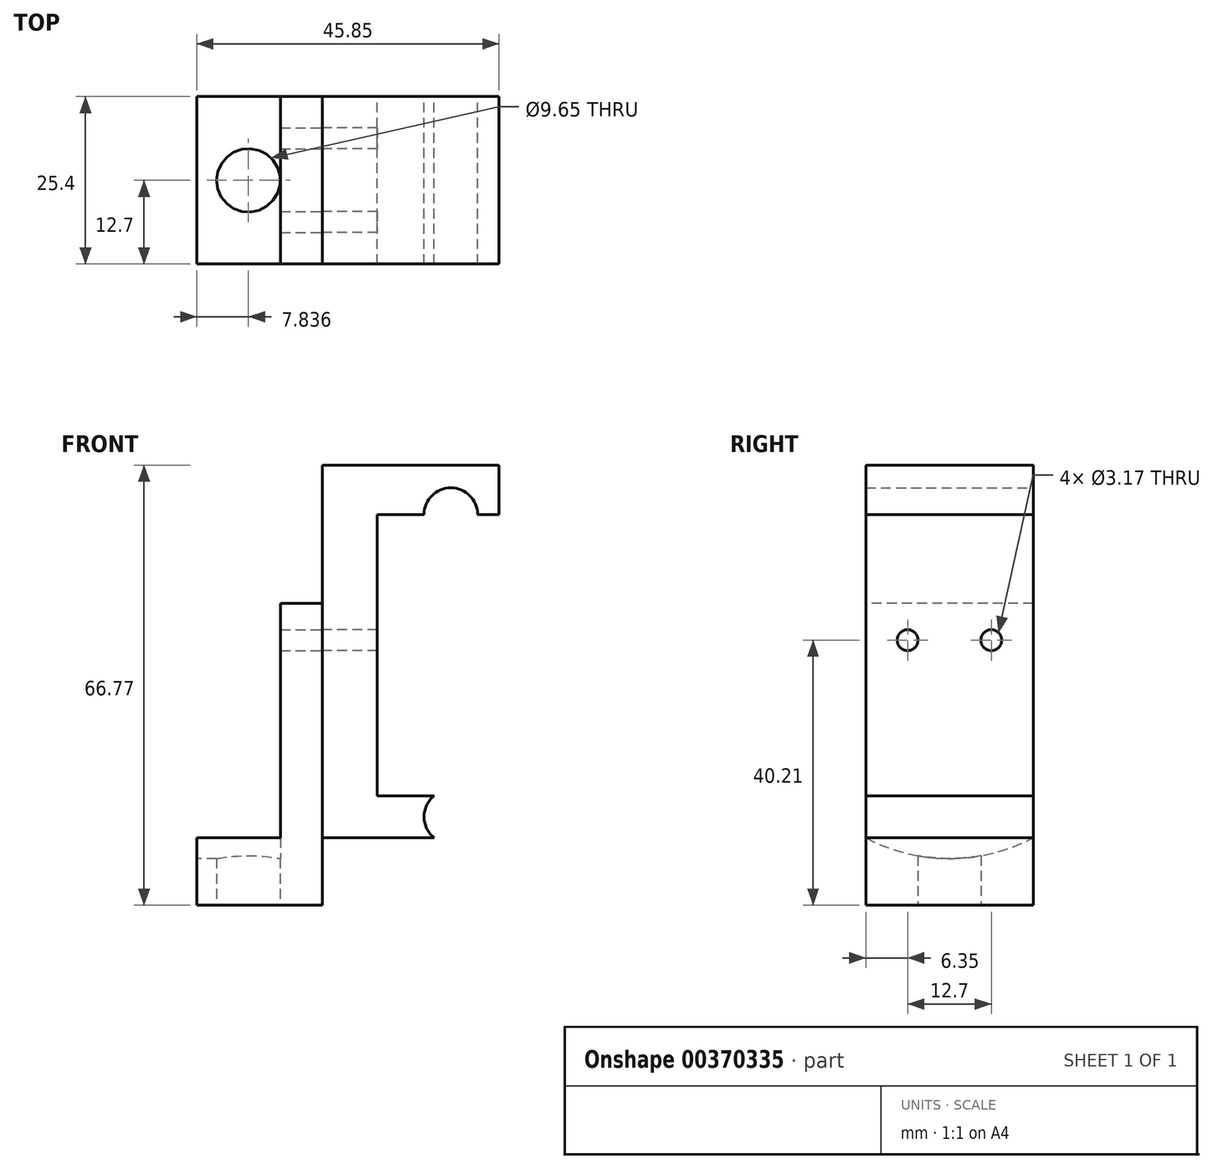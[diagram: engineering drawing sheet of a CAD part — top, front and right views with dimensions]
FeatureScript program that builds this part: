
annotation { "Feature Type Name" : "Feature", "Feature Type Description" : "" }
export const myFeature = defineFeature(function(context is Context, id is Id, definition is map)
    precondition{}
    {
        {
            var Q0;
            Q0=qCreatedBy(makeId("Front.planeOp"),FACE);
            var sketch = newSketch(context, id + "F0", { "sketchPlane" : qUnion([Q0])});
            skCircle(sketch, "E0", {"center": v(0, 0) * mm, "radius": 4.06 * mm, "construction": true});
            skCircle(sketch, "E1", {"center": v(0, -45.85) * mm, "radius": 4.06 * mm, "construction": true});
            skLineSegment(sketch, "E2", {"start": v(4.06, 0) * mm, "end": v(7.3, 0) * mm});
            skLineSegment(sketch, "E3", {"start": v(7.3, 0) * mm, "end": v(7.3, 7.51) * mm});
            skArc(sketch, "E4", {"start": v(4.06, 0) * mm, "mid": v(0, 4.06) * mm, "end": v(-4.06, 0) * mm});
            skLineSegment(sketch, "E5", {"start": v(-2.52, -42.66) * mm, "end": v(-2.52, -49.04) * mm, "construction": true});
            skArc(sketch, "E6", {"start": v(-2.52, -42.66) * mm, "mid": v(-4.06, -45.85) * mm, "end": v(-2.52, -49.04) * mm});
            skLineSegment(sketch, "E7", {"start": v(-2.52, -42.66) * mm, "end": v(-11.15, -42.66) * mm});
            skLineSegment(sketch, "E8", {"start": v(-11.15, -42.66) * mm, "end": v(-11.15, 0) * mm});
            skLineSegment(sketch, "E9", {"start": v(-11.15, 0) * mm, "end": v(-4.06, 0) * mm});
            skLineSegment(sketch, "E10", {"start": v(7.3, 7.51) * mm, "end": v(-19.5, 7.51) * mm});
            skLineSegment(sketch, "E11", {"start": v(-19.5, 7.51) * mm, "end": v(-19.5, -49.04) * mm});
            skLineSegment(sketch, "E12", {"start": v(-19.5, -49.04) * mm, "end": v(-2.52, -49.04) * mm});
            skSolve(sketch);
        }
        {
            var Q0;
            Q0 = qSketchRegion(id + "F0", true);
            extrude(context, id + "F1", {"entities" : qUnion([Q0]), "endBound" : BoundingType.SYMMETRIC, "depth" : 25.4 * mm});
        }
        {
            var Q0;
            Q0=makeQuery(id+"F1.opExtrude","SWEPT_FACE",FACE,{"disambiguationData":[OSD([sQuery(id+"F0.wireOp",EDGE,"E11")])]});
            var sketch = newSketch(context, id + "F2", { "sketchPlane" : qUnion([Q0])});
            skCircle(sketch, "E13", {"center": v(-6.35, -19.05) * mm, "radius": 1.59 * mm});
            skCircle(sketch, "E14", {"center": v(6.35, -19.05) * mm, "radius": 1.59 * mm});
            skSolve(sketch);
        }
        {
            var Q0;
            Q0 = qSketchRegion(id + "F2", true);
            extrude(context, id + "F3", {"entities" : qUnion([Q0]), "operationType" : NewBodyOperationType.REMOVE, "endBound" : BoundingType.THROUGH_ALL, "oppositeDirection" : true, "depth" : 25.4 * mm});
        }
        {
            var Q0;
            Q0=makeQuery(id+"F1.opExtrude","SWEPT_FACE",FACE,{"disambiguationData":[OSD([sQuery(id+"F0.wireOp",EDGE,"E11")])]});
            var sketch = newSketch(context, id + "F4", { "sketchPlane" : qUnion([Q0])});
            skLineSegment(sketch, "E15.bottom", {"start": v(-12.7, -13.48) * mm, "end": v(12.7, -13.48) * mm});
            skLineSegment(sketch, "E15.top", {"start": v(-12.7, -59.26) * mm, "end": v(12.7, -59.26) * mm});
            skLineSegment(sketch, "E15.left", {"start": v(-12.7, -13.48) * mm, "end": v(-12.7, -59.26) * mm});
            skLineSegment(sketch, "E15.right", {"start": v(12.7, -13.48) * mm, "end": v(12.7, -59.26) * mm});
            skCircle(sketch, "E16", {"center": v(-6.35, -19.05) * mm, "radius": 1.59 * mm});
            skCircle(sketch, "E17", {"center": v(6.35, -19.05) * mm, "radius": 1.59 * mm});
            skSolve(sketch);
        }
        {
            var Q0;
            Q0 = qSketchRegion(id + "F4", true);
            extrude(context, id + "F5", {"entities" : qUnion([Q0]), "depth" : 19.05 * mm});
        }
        {
            var Q0;
            Q0=makeQuery(id+"F5.opExtrude","CAP_FACE",FACE,{"disambiguationData":[OSD([sQuery(id+"F4.wireOp",EDGE,"E15.bottom"),sQuery(id+"F4.wireOp",EDGE,"E15.top"),sQuery(id+"F4.wireOp",EDGE,"E15.left"),sQuery(id+"F4.wireOp",EDGE,"E15.right"),sQuery(id+"F4.wireOp",EDGE,"E16"),sQuery(id+"F4.wireOp",EDGE,"E17")])],"isStart":false});
            var sketch = newSketch(context, id + "F6", { "sketchPlane" : qUnion([Q0])});
            skCircle(sketch, "E18", {"center": v(0, -24.88) * mm, "radius": 27.3 * mm});
            skSolve(sketch);
        }
        {
            var Q0;
            Q0 = qSketchRegion(id + "F6", true);
            var Q1;
            Q1=makeQuery(id+"F1.opExtrude","SWEPT_FACE",FACE,{"disambiguationData":[OSD([sQuery(id+"F0.wireOp",EDGE,"E11")])]});
            extrude(context, id + "F7", {"entities" : qUnion([Q0]), "operationType" : NewBodyOperationType.REMOVE, "oppositeDirection" : true, "endBoundEntityFace" : qUnion([Q1]), "depth" : 12.7 * mm});
        }
        {
            var Q0;
            Q0=makeQuery(id+"F5.opExtrude","SWEPT_FACE",FACE,{"disambiguationData":[OSD([sQuery(id+"F4.wireOp",EDGE,"E15.top")])]});
            var sketch = newSketch(context, id + "F8", { "sketchPlane" : qUnion([Q0])});
            skCircle(sketch, "E19", {"center": v(-30.71, 0) * mm, "radius": 4.83 * mm});
            skSolve(sketch);
        }
        {
            var Q0;
            Q0 = qSketchRegion(id + "F8", true);
            extrude(context, id + "F9", {"entities" : qUnion([Q0]), "operationType" : NewBodyOperationType.REMOVE, "oppositeDirection" : true, "depth" : 12.7 * mm});
        }
    });
